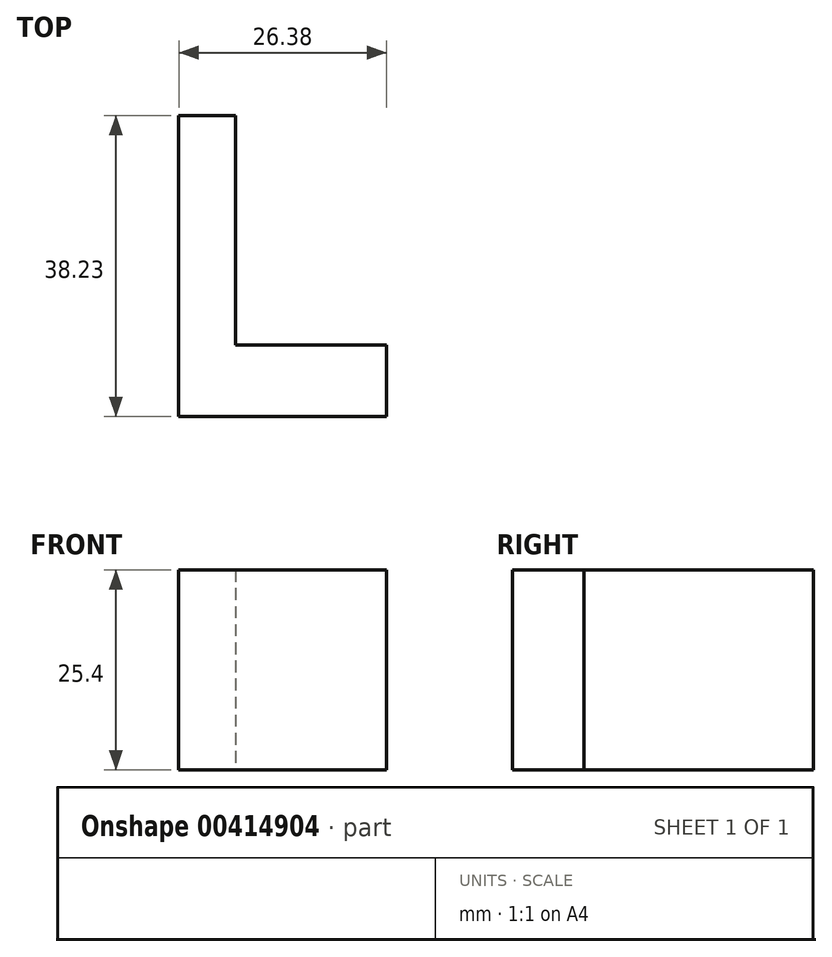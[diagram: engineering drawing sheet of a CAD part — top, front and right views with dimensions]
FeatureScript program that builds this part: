
annotation { "Feature Type Name" : "Feature", "Feature Type Description" : "" }
export const myFeature = defineFeature(function(context is Context, id is Id, definition is map)
    precondition{}
    {
        {
            var Q0;
            Q0=qCreatedBy(makeId("Top.planeOp"),FACE);
            var sketch = newSketch(context, id + "F0", { "sketchPlane" : qUnion([Q0])});
            skLineSegment(sketch, "E0", {"start": v(-48.5, 57.58) * mm, "end": v(-48.5, 19.35) * mm});
            skLineSegment(sketch, "E1", {"start": v(-48.5, 19.35) * mm, "end": v(-22.12, 19.35) * mm});
            skLineSegment(sketch, "E2", {"start": v(-22.12, 19.35) * mm, "end": v(-22.12, 28.43) * mm});
            skLineSegment(sketch, "E3", {"start": v(-22.12, 28.43) * mm, "end": v(-41.31, 28.43) * mm});
            skLineSegment(sketch, "E4", {"start": v(-41.31, 28.43) * mm, "end": v(-41.31, 57.58) * mm});
            skLineSegment(sketch, "E5", {"start": v(-41.31, 57.58) * mm, "end": v(-48.5, 57.58) * mm});
            skSolve(sketch);
        }
        {
            var Q0;
            Q0=makeQuery(id+"F0.imprint","IMPRINT",FACE,{"disambiguationData":[TD([[makeQuery(id+"F0.imprint","IMPRINT",EDGE,{"derivedFrom":sQuery(id+"F0.wireOp",EDGE,"E0")}),1.0]])]});
            extrude(context, id + "F1", {"entities" : qUnion([Q0]), "depth" : 25.4 * mm});
        }
    });
